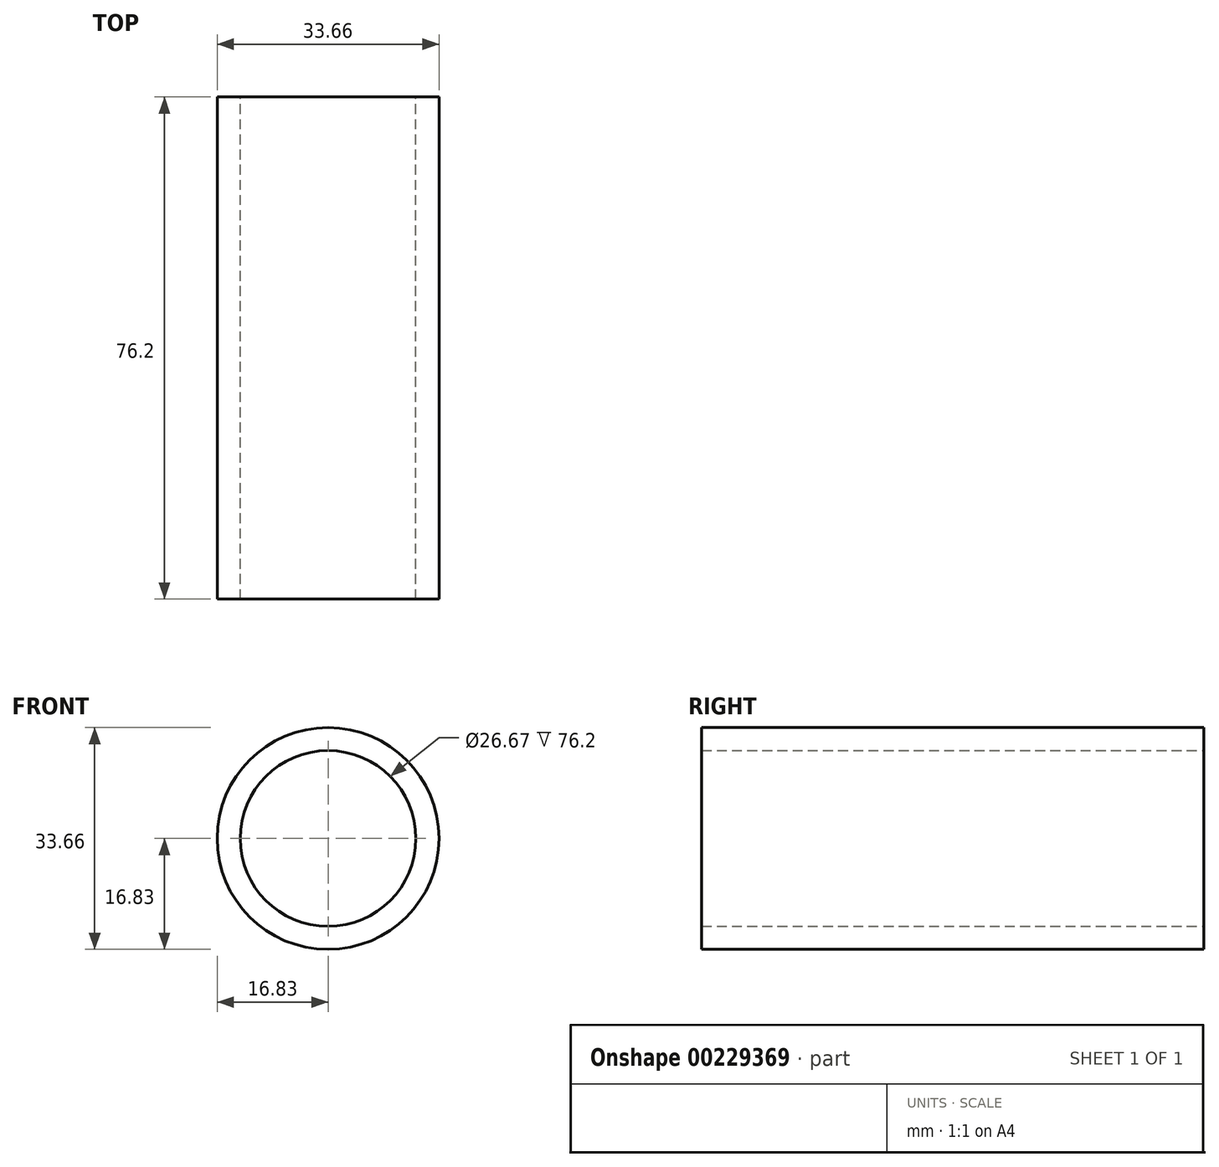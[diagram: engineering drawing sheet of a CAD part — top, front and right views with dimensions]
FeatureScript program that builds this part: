
annotation { "Feature Type Name" : "Feature", "Feature Type Description" : "" }
export const myFeature = defineFeature(function(context is Context, id is Id, definition is map)
    precondition{}
    {
        {
            var Q0;
            Q0=qCreatedBy(makeId("Front.planeOp"),FACE);
            var sketch = newSketch(context, id + "F0", { "sketchPlane" : qUnion([Q0])});
            skCircle(sketch, "E0", {"center": v(0, 0) * mm, "radius": 13.34 * mm});
            skCircle(sketch, "E1", {"center": v(0, 0) * mm, "radius": 16.83 * mm});
            skSolve(sketch);
        }
        {
            var Q0;
            Q0=makeQuery(id+"F0.imprint","IMPRINT",FACE,{"disambiguationData":[TD([[makeQuery(id+"F0.imprint","IMPRINT",EDGE,{"derivedFrom":sQuery(id+"F0.wireOp",EDGE,"E0")}),-1.0]])]});
            extrude(context, id + "F1", {"entities" : qUnion([Q0]), "depth" : 76.2 * mm});
        }
    });
